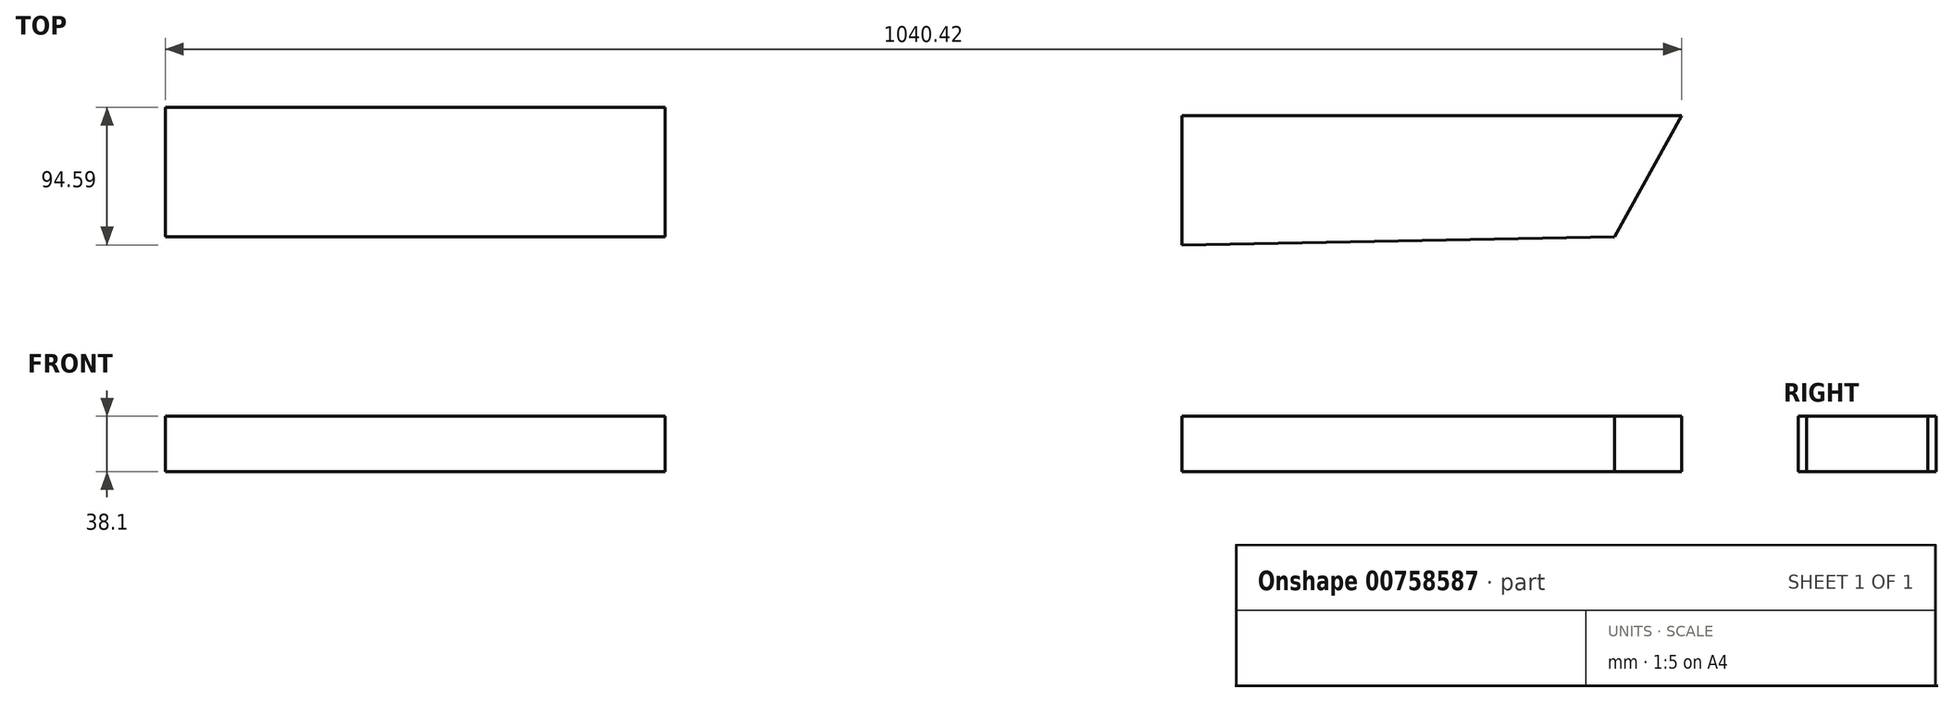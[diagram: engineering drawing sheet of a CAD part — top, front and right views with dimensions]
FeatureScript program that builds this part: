
annotation { "Feature Type Name" : "Feature", "Feature Type Description" : "" }
export const myFeature = defineFeature(function(context is Context, id is Id, definition is map)
    precondition{}
    {
        {
            var Q0;
            Q0=qCreatedBy(makeId("Top.planeOp"),FACE);
            var sketch = newSketch(context, id + "F0", { "sketchPlane" : qUnion([Q0])});
            skLineSegment(sketch, "E0", {"start": v(0, 0) * mm, "end": v(45.94, 83.21) * mm});
            skLineSegment(sketch, "E1", {"start": v(45.94, 83.21) * mm, "end": v(-296.96, 83.21) * mm});
            skLineSegment(sketch, "E2", {"start": v(-296.96, 83.21) * mm, "end": v(-296.96, -5.69) * mm});
            skLineSegment(sketch, "E3", {"start": v(-296.96, -5.69) * mm, "end": v(0, 0) * mm});
            skLineSegment(sketch, "E4.bottom", {"start": v(-994.48, 88.9) * mm, "end": v(-651.58, 88.9) * mm});
            skLineSegment(sketch, "E4.top", {"start": v(-994.48, 0) * mm, "end": v(-651.58, 0) * mm});
            skLineSegment(sketch, "E4.left", {"start": v(-994.48, 88.9) * mm, "end": v(-994.48, 0) * mm});
            skLineSegment(sketch, "E4.right", {"start": v(-651.58, 88.9) * mm, "end": v(-651.58, 0) * mm});
            skSolve(sketch);
        }
        {
            var Q0;
            Q0=makeQuery(id+"F0.imprint","IMPRINT",FACE,{"disambiguationData":[TD([[makeQuery(id+"F0.imprint","IMPRINT",EDGE,{"derivedFrom":sQuery(id+"F0.wireOp",EDGE,"YIdYByoj-Dhbe-Mf2R-w79Z-LfYU1aW7UFA9")}),-1.0]])]});
            var Q1;
            Q1=makeQuery(id+"F0.imprint","IMPRINT",FACE,{"disambiguationData":[TD([[makeQuery(id+"F0.imprint","IMPRINT",EDGE,{"derivedFrom":sQuery(id+"F0.wireOp",EDGE,"E0")}),1.0]])]});
            extrude(context, id + "F1", {"entities" : qUnion([Q0, Q1]), "endBound" : BoundingType.SYMMETRIC, "depth" : 38.1 * mm, "offsetDistance" : 25.4 * mm});
        }
        {
            var Q0;
            Q0=makeQuery(id+"F0.imprint","IMPRINT",FACE,{"disambiguationData":[TD([[makeQuery(id+"F0.imprint","IMPRINT",EDGE,{"derivedFrom":sQuery(id+"F0.wireOp",EDGE,"E4.bottom")}),-1.0]])]});
            extrude(context, id + "F2", {"entities" : qUnion([Q0]), "endBound" : BoundingType.SYMMETRIC, "depth" : 38.1 * mm, "offsetDistance" : 25.4 * mm});
        }
    });
